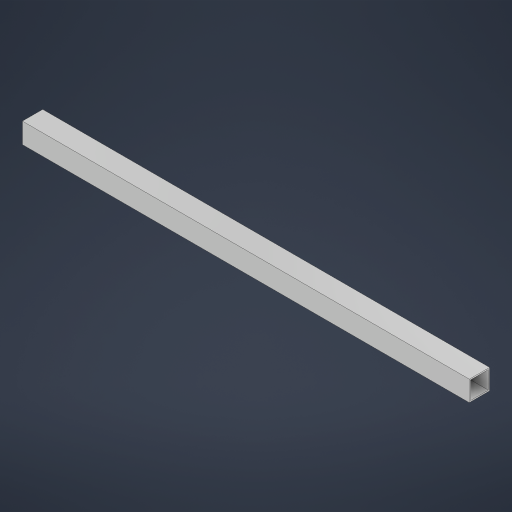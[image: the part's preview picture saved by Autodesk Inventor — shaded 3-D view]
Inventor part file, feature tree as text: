
AUTODESK INVENTOR PART (.ipt)
format: ipt  version: 2024 (Build 280153000, 153)  size: 177,152 bytes
history: native  units: in
note: dims shown in document units (in); Inventor stores cm internally (conversion verified against a paired STEP export)
features: extrude x1, sketch x1
ambient origin geometry x8: Origin, YZ Plane, XZ Plane, XY Plane, X Axis, Y Axis, Z Axis, Center Point
bodies: Solid1 (feature_tree)
feature tree (2):
  extrude  "Extrusion1"  Depth=1.0in
  sketch  "Sketch1"  dims[d0=1.0in d1=1.0in d2=0.0625in d3=0.0625in d4=0.0625in d5=0.0625in d6=22.0in d7=0.0in]
